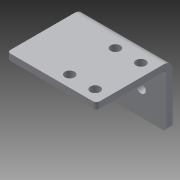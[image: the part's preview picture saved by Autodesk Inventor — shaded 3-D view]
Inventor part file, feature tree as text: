
AUTODESK INVENTOR PART (.ipt)
format: ipt  version: 2014 (Build 180170000, 170)  size: 190,464 bytes
history: native  units: in
note: dims shown in document units (in); Inventor stores cm internally (conversion verified against a paired STEP export)
features: sheet_metal_op x4, other x4, sketch x3, fillet x1, extrude x1
ambient origin geometry x8: Origin, YZ Plane, XZ Plane, XY Plane, X Axis, Y Axis, Z Axis, Center Point
bodies: Solid1 (feature_tree)
feature tree (13):
  sheet_metal_op  "Face1"
  sheet_metal_op  "Flange1"
  fillet  "Fillet1"  Radius=1.75in
  extrude  "Extrusion1"  Depth=0.19in
  sketch  "Sketch1"  dims[d1=1.0in d2=0.19in]
  other  "Plate1"
  sketch  "Sketch2"  dims[d4=0.7874in d6=1.0in d7=0.3937in d9=1.0in]
  other  "Plate2"
  sheet_metal_op  "Bend1"
  sheet_metal_op  "Corner1"
  sketch  "Sketch3"  dims[d11=0.125in d12=0.125in d13=0.0625in d14=0.25in d15=0.125in d16=1.5in d17=90.0deg d18=0.05in d19=0.5in d20=0.125in d21=0.125in d22=0.0625in d23=1.35in d24=0.75in d27=0.19in d28=0.125in d29=0.2265in d30=1.0in d31=0.0in d34=0.25in d35=0.875in d3=0.0in]
  other  "Definition1"
  other  "Cut1"
